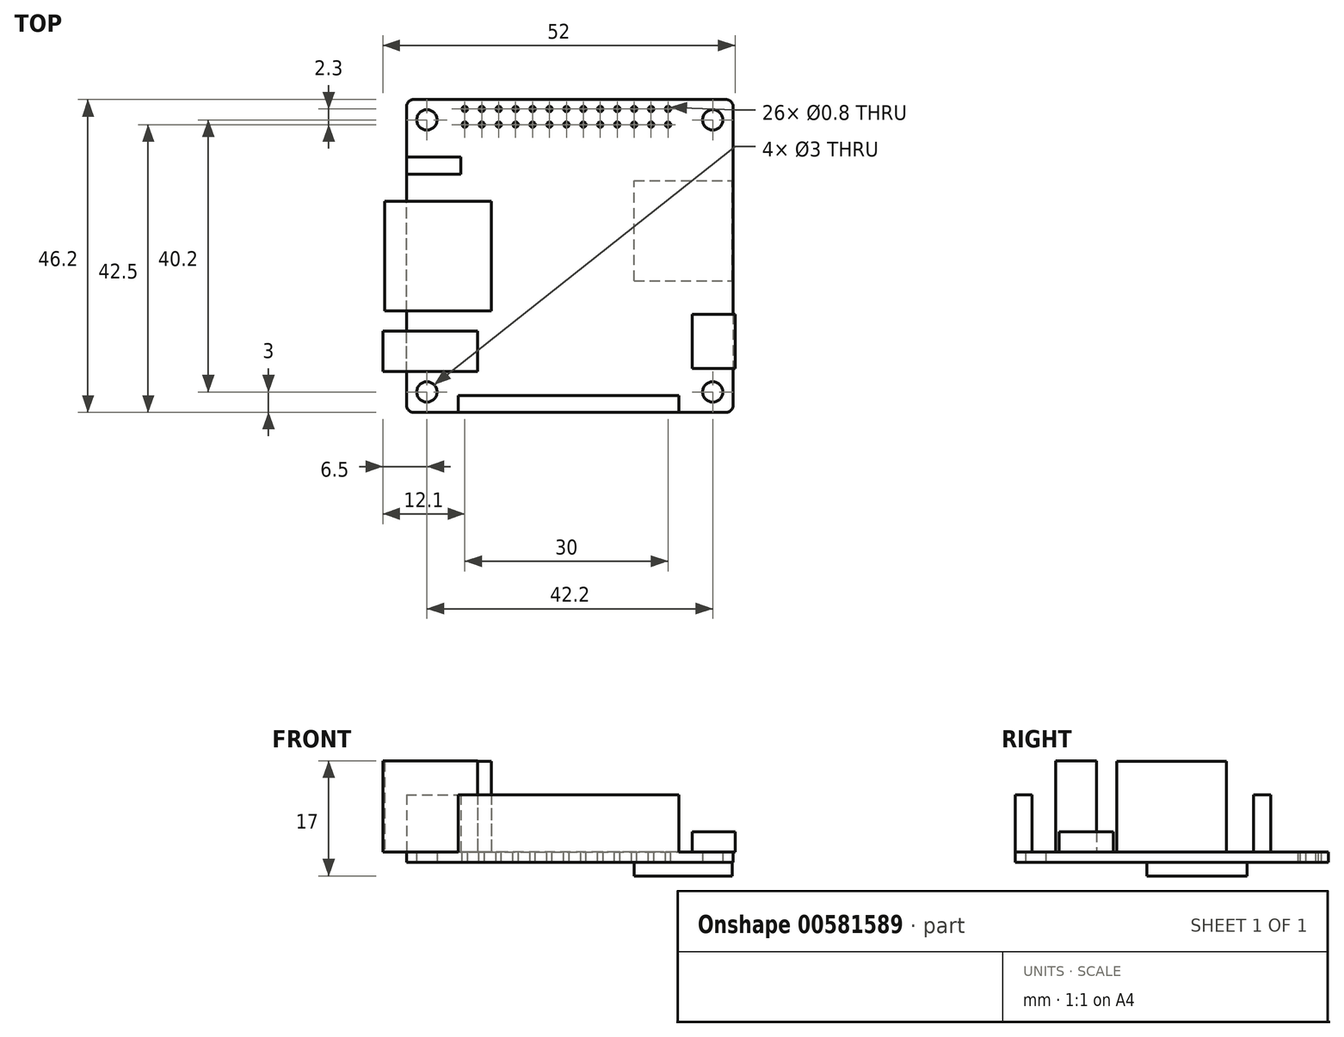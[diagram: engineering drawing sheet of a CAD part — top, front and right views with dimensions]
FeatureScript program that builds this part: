
annotation { "Feature Type Name" : "Feature", "Feature Type Description" : "" }
export const myFeature = defineFeature(function(context is Context, id is Id, definition is map)
    precondition{}
    {
        {
            var Q0;
            Q0=qCreatedBy(makeId("Top.planeOp"),FACE);
            var sketch = newSketch(context, id + "F0", { "sketchPlane" : qUnion([Q0])});
            skLineSegment(sketch, "E0.bottom", {"start": v(23.1, -23.1) * mm, "end": v(-23.1, -23.1) * mm});
            skLineSegment(sketch, "E0.top", {"start": v(23.1, 23.1) * mm, "end": v(-23.1, 23.1) * mm});
            skLineSegment(sketch, "E0.left", {"start": v(24.1, -22.1) * mm, "end": v(24.1, 22.1) * mm});
            skLineSegment(sketch, "E0.right", {"start": v(-24.1, -22.1) * mm, "end": v(-24.1, 22.1) * mm});
            skPoint(sketch, "E0.middle", {"position": v(0, 0) * mm});
            skPoint(sketch, "E1.visualSharp", {"position": v(-24.1, 23.1) * mm});
            skArc(sketch, "E1.filletArc", {"start": v(-23.1, 23.1) * mm, "mid": v(-23.8, 22.8) * mm, "end": v(-24.1, 22.1) * mm});
            skPoint(sketch, "E2.visualSharp", {"position": v(24.1, 23.1) * mm});
            skArc(sketch, "E2.filletArc", {"start": v(24.1, 22.1) * mm, "mid": v(23.8, 22.8) * mm, "end": v(23.1, 23.1) * mm});
            skPoint(sketch, "E3.visualSharp", {"position": v(24.1, -23.1) * mm});
            skArc(sketch, "E3.filletArc", {"start": v(23.1, -23.1) * mm, "mid": v(23.8, -22.8) * mm, "end": v(24.1, -22.1) * mm});
            skPoint(sketch, "E4.visualSharp", {"position": v(-24.1, -23.1) * mm});
            skArc(sketch, "E4.filletArc", {"start": v(-24.1, -22.1) * mm, "mid": v(-23.8, -22.8) * mm, "end": v(-23.1, -23.1) * mm});
            skCircle(sketch, "E5", {"center": v(-21.1, 20.1) * mm, "radius": 1.5 * mm});
            skCircle(sketch, "E6", {"center": v(21.1, 20.1) * mm, "radius": 1.5 * mm});
            skCircle(sketch, "E7", {"center": v(21.1, -20.1) * mm, "radius": 1.5 * mm});
            skCircle(sketch, "E8", {"center": v(-21.1, -20.1) * mm, "radius": 1.5 * mm});
            skSolve(sketch);
        }
        {
            var Q0;
            Q0=makeQuery(id+"F0.imprint","IMPRINT",FACE,{"disambiguationData":[TD([[makeQuery(id+"F0.imprint","IMPRINT",EDGE,{"derivedFrom":sQuery(id+"F0.wireOp",EDGE,"E0.bottom")}),-1.0]])]});
            extrude(context, id + "F1", {"entities" : qUnion([Q0]), "depth" : 1.5 * mm, "offsetDistance" : 25 * mm});
        }
        {
            var Q0;
            Q0=makeQuery(id+"F1.opExtrude","CAP_FACE",FACE,{"disambiguationData":[OSD([sQuery(id+"F0.wireOp",EDGE,"E0.bottom"),sQuery(id+"F0.wireOp",EDGE,"E0.top"),sQuery(id+"F0.wireOp",EDGE,"E0.left"),sQuery(id+"F0.wireOp",EDGE,"E0.right"),sQuery(id+"F0.wireOp",EDGE,"E1.filletArc"),sQuery(id+"F0.wireOp",EDGE,"E2.filletArc"),sQuery(id+"F0.wireOp",EDGE,"E3.filletArc"),sQuery(id+"F0.wireOp",EDGE,"E4.filletArc"),sQuery(id+"F0.wireOp",EDGE,"E5"),sQuery(id+"F0.wireOp",EDGE,"E6"),sQuery(id+"F0.wireOp",EDGE,"E7"),sQuery(id+"F0.wireOp",EDGE,"E8")])],"isStart":false});
            var sketch = newSketch(context, id + "F2", { "sketchPlane" : qUnion([Q0])});
            skLineSegment(sketch, "E9.bottom", {"start": v(-16.5, -23.1) * mm, "end": v(16.1, -23.1) * mm});
            skLineSegment(sketch, "E9.top", {"start": v(-16.5, -20.6) * mm, "end": v(16.1, -20.6) * mm});
            skLineSegment(sketch, "E9.left", {"start": v(-16.5, -23.1) * mm, "end": v(-16.5, -20.6) * mm});
            skLineSegment(sketch, "E9.right", {"start": v(16.1, -23.1) * mm, "end": v(16.1, -20.6) * mm});
            skSolve(sketch);
        }
        {
            var Q0;
            Q0=makeQuery(id+"F2.imprint","IMPRINT",FACE,{"disambiguationData":[TD([[makeQuery(id+"F2.imprint","IMPRINT",EDGE,{"derivedFrom":sQuery(id+"F2.wireOp",EDGE,"E9.bottom")}),-1.0]])]});
            extrude(context, id + "F3", {"entities" : qUnion([Q0]), "operationType" : NewBodyOperationType.ADD, "depth" : 8.5 * mm, "offsetDistance" : 25 * mm});
        }
        {
            var Q0;
            Q0=makeQuery(id+"F1.opExtrude","CAP_FACE",FACE,{"disambiguationData":[OSD([sQuery(id+"F0.wireOp",EDGE,"E0.bottom"),sQuery(id+"F0.wireOp",EDGE,"E0.top"),sQuery(id+"F0.wireOp",EDGE,"E0.left"),sQuery(id+"F0.wireOp",EDGE,"E0.right"),sQuery(id+"F0.wireOp",EDGE,"E1.filletArc"),sQuery(id+"F0.wireOp",EDGE,"E2.filletArc"),sQuery(id+"F0.wireOp",EDGE,"E3.filletArc"),sQuery(id+"F0.wireOp",EDGE,"E4.filletArc"),sQuery(id+"F0.wireOp",EDGE,"E5"),sQuery(id+"F0.wireOp",EDGE,"E6"),sQuery(id+"F0.wireOp",EDGE,"E7"),sQuery(id+"F0.wireOp",EDGE,"E8")])],"isStart":false});
            var sketch = newSketch(context, id + "F4", { "sketchPlane" : qUnion([Q0])});
            skLineSegment(sketch, "E10.bottom", {"start": v(24.1, -8.6) * mm, "end": v(18.1, -8.6) * mm});
            skLineSegment(sketch, "E10.top", {"start": v(24.1, -16.6) * mm, "end": v(18.1, -16.6) * mm});
            skLineSegment(sketch, "E10.left", {"start": v(24.1, -8.6) * mm, "end": v(24.1, -16.6) * mm});
            skLineSegment(sketch, "E10.right", {"start": v(18.1, -8.6) * mm, "end": v(18.1, -16.6) * mm});
            skSolve(sketch);
        }
        {
            var Q0;
            Q0=makeQuery(id+"F4.imprint","IMPRINT",FACE,{"disambiguationData":[TD([[makeQuery(id+"F4.imprint","IMPRINT",EDGE,{"derivedFrom":sQuery(id+"F4.wireOp",EDGE,"E10.bottom")}),1.0]])]});
            extrude(context, id + "F5", {"entities" : qUnion([Q0]), "operationType" : NewBodyOperationType.ADD, "depth" : 3 * mm, "offsetDistance" : 25 * mm});
        }
        {
            var Q0;
            Q0=makeQuery(id+"F5.boolean.opBoolean","MERGE",FACE,{"derivedFrom":[makeQuery(id+"F1.opExtrude","SWEPT_FACE",FACE,{"disambiguationData":[OSD([sQuery(id+"F0.wireOp",EDGE,"E0.left")])]}),makeQuery(id+"F5.opExtrude","SWEPT_FACE",FACE,{"disambiguationData":[OSD([sQuery(id+"F4.wireOp",EDGE,"E10.left")])]})]});
            var sketch = newSketch(context, id + "F6", { "sketchPlane" : qUnion([Q0])});
            skLineSegment(sketch, "E11", {"start": v(-8.6, 1.5) * mm, "end": v(-16.6, 1.5) * mm});
            skSolve(sketch);
        }
        {
            var Q0;
            Q0=makeQuery(id+"F6.imprint","IMPRINT",FACE,{"disambiguationData":[TD([[makeQuery(id+"F6.imprint","IMPRINT",EDGE,{"derivedFrom":sQuery(id+"F6.wireOp",EDGE,"E11")}),-1.0]])]});
            extrude(context, id + "F7", {"entities" : qUnion([Q0]), "operationType" : NewBodyOperationType.ADD, "depth" : 0.3 * mm, "offsetDistance" : 25 * mm});
        }
        {
            var Q0;
            Q0=makeQuery(id+"F1.opExtrude","CAP_FACE",FACE,{"disambiguationData":[OSD([sQuery(id+"F0.wireOp",EDGE,"E0.bottom"),sQuery(id+"F0.wireOp",EDGE,"E0.top"),sQuery(id+"F0.wireOp",EDGE,"E0.left"),sQuery(id+"F0.wireOp",EDGE,"E0.right"),sQuery(id+"F0.wireOp",EDGE,"E1.filletArc"),sQuery(id+"F0.wireOp",EDGE,"E2.filletArc"),sQuery(id+"F0.wireOp",EDGE,"E3.filletArc"),sQuery(id+"F0.wireOp",EDGE,"E4.filletArc"),sQuery(id+"F0.wireOp",EDGE,"E5"),sQuery(id+"F0.wireOp",EDGE,"E6"),sQuery(id+"F0.wireOp",EDGE,"E7"),sQuery(id+"F0.wireOp",EDGE,"E8")])],"isStart":false});
            var sketch = newSketch(context, id + "F8", { "sketchPlane" : qUnion([Q0])});
            skLineSegment(sketch, "E12.bottom", {"start": v(-16.4, 23.1) * mm, "end": v(16.1, 23.1) * mm});
            skLineSegment(sketch, "E12.top", {"start": v(-16.4, 18.1) * mm, "end": v(16.1, 18.1) * mm});
            skLineSegment(sketch, "E12.left", {"start": v(-16.4, 23.1) * mm, "end": v(-16.4, 18.1) * mm});
            skLineSegment(sketch, "E12.right", {"start": v(16.1, 23.1) * mm, "end": v(16.1, 18.1) * mm});
            skCircle(sketch, "E13", {"center": v(-15.5, 21.7) * mm, "radius": 0.4 * mm});
            skCircle(sketch, "E14", {"center": v(-15.5, 19.4) * mm, "radius": 0.4 * mm});
            skCircle(sketch, "E15.1.0.0", {"center": v(-13, 21.7) * mm, "radius": 0.4 * mm});
            skCircle(sketch, "E15.1.0.1", {"center": v(-13, 19.4) * mm, "radius": 0.4 * mm});
            skCircle(sketch, "E15.2.0.0", {"center": v(-10.5, 21.7) * mm, "radius": 0.4 * mm});
            skCircle(sketch, "E15.2.0.1", {"center": v(-10.5, 19.4) * mm, "radius": 0.4 * mm});
            skCircle(sketch, "E15.3.0.0", {"center": v(-8, 21.7) * mm, "radius": 0.4 * mm});
            skCircle(sketch, "E15.3.0.1", {"center": v(-8, 19.4) * mm, "radius": 0.4 * mm});
            skCircle(sketch, "E15.4.0.0", {"center": v(-5.5, 21.7) * mm, "radius": 0.4 * mm});
            skCircle(sketch, "E15.4.0.1", {"center": v(-5.5, 19.4) * mm, "radius": 0.4 * mm});
            skCircle(sketch, "E15.5.0.0", {"center": v(-3, 21.7) * mm, "radius": 0.4 * mm});
            skCircle(sketch, "E15.5.0.1", {"center": v(-3, 19.4) * mm, "radius": 0.4 * mm});
            skCircle(sketch, "E15.6.0.0", {"center": v(-0.5, 21.7) * mm, "radius": 0.4 * mm});
            skCircle(sketch, "E15.6.0.1", {"center": v(-0.5, 19.4) * mm, "radius": 0.4 * mm});
            skCircle(sketch, "E15.7.0.0", {"center": v(2, 21.7) * mm, "radius": 0.4 * mm});
            skCircle(sketch, "E15.7.0.1", {"center": v(2, 19.4) * mm, "radius": 0.4 * mm});
            skCircle(sketch, "E15.8.0.0", {"center": v(4.5, 21.7) * mm, "radius": 0.4 * mm});
            skCircle(sketch, "E15.8.0.1", {"center": v(4.5, 19.4) * mm, "radius": 0.4 * mm});
            skCircle(sketch, "E15.9.0.0", {"center": v(7, 21.7) * mm, "radius": 0.4 * mm});
            skCircle(sketch, "E15.9.0.1", {"center": v(7, 19.4) * mm, "radius": 0.4 * mm});
            skCircle(sketch, "E15.10.0.0", {"center": v(9.5, 21.7) * mm, "radius": 0.4 * mm});
            skCircle(sketch, "E15.10.0.1", {"center": v(9.5, 19.4) * mm, "radius": 0.4 * mm});
            skCircle(sketch, "E15.11.0.0", {"center": v(12, 21.7) * mm, "radius": 0.4 * mm});
            skCircle(sketch, "E15.11.0.1", {"center": v(12, 19.4) * mm, "radius": 0.4 * mm});
            skCircle(sketch, "E15.12.0.0", {"center": v(14.5, 21.7) * mm, "radius": 0.4 * mm});
            skCircle(sketch, "E15.12.0.1", {"center": v(14.5, 19.4) * mm, "radius": 0.4 * mm});
            skLineSegment(sketch, "E15.direction1", {"start": v(-15.5, 19.4) * mm, "end": v(-13, 19.4) * mm, "construction": true});
            skSolve(sketch);
        }
        {
            var Q0;
            Q0=makeQuery(id+"F8.imprint","IMPRINT",FACE,{"disambiguationData":[TD([[makeQuery(id+"F8.imprint","IMPRINT",EDGE,{"derivedFrom":sQuery(id+"F8.wireOp",EDGE,"E15.1.0.0")}),1.0]])]});
            var Q1;
            Q1=makeQuery(id+"F8.imprint","IMPRINT",FACE,{"disambiguationData":[TD([[makeQuery(id+"F8.imprint","IMPRINT",EDGE,{"derivedFrom":sQuery(id+"F8.wireOp",EDGE,"E13")}),1.0]])]});
            var Q2;
            Q2=makeQuery(id+"F8.imprint","IMPRINT",FACE,{"disambiguationData":[TD([[makeQuery(id+"F8.imprint","IMPRINT",EDGE,{"derivedFrom":sQuery(id+"F8.wireOp",EDGE,"E15.2.0.0")}),1.0]])]});
            var Q3;
            Q3=makeQuery(id+"F8.imprint","IMPRINT",FACE,{"disambiguationData":[TD([[makeQuery(id+"F8.imprint","IMPRINT",EDGE,{"derivedFrom":sQuery(id+"F8.wireOp",EDGE,"E15.3.0.0")}),1.0]])]});
            var Q4;
            Q4=makeQuery(id+"F8.imprint","IMPRINT",FACE,{"disambiguationData":[TD([[makeQuery(id+"F8.imprint","IMPRINT",EDGE,{"derivedFrom":sQuery(id+"F8.wireOp",EDGE,"E15.4.0.0")}),1.0]])]});
            var Q5;
            Q5=makeQuery(id+"F8.imprint","IMPRINT",FACE,{"disambiguationData":[TD([[makeQuery(id+"F8.imprint","IMPRINT",EDGE,{"derivedFrom":sQuery(id+"F8.wireOp",EDGE,"E15.5.0.0")}),1.0]])]});
            var Q6;
            Q6=makeQuery(id+"F8.imprint","IMPRINT",FACE,{"disambiguationData":[TD([[makeQuery(id+"F8.imprint","IMPRINT",EDGE,{"derivedFrom":sQuery(id+"F8.wireOp",EDGE,"E15.6.0.0")}),1.0]])]});
            var Q7;
            Q7=makeQuery(id+"F8.imprint","IMPRINT",FACE,{"disambiguationData":[TD([[makeQuery(id+"F8.imprint","IMPRINT",EDGE,{"derivedFrom":sQuery(id+"F8.wireOp",EDGE,"E15.7.0.0")}),1.0]])]});
            var Q8;
            Q8=makeQuery(id+"F8.imprint","IMPRINT",FACE,{"disambiguationData":[TD([[makeQuery(id+"F8.imprint","IMPRINT",EDGE,{"derivedFrom":sQuery(id+"F8.wireOp",EDGE,"E15.8.0.0")}),1.0]])]});
            var Q9;
            Q9=makeQuery(id+"F8.imprint","IMPRINT",FACE,{"disambiguationData":[TD([[makeQuery(id+"F8.imprint","IMPRINT",EDGE,{"derivedFrom":sQuery(id+"F8.wireOp",EDGE,"E15.9.0.0")}),1.0]])]});
            var Q10;
            Q10=makeQuery(id+"F8.imprint","IMPRINT",FACE,{"disambiguationData":[TD([[makeQuery(id+"F8.imprint","IMPRINT",EDGE,{"derivedFrom":sQuery(id+"F8.wireOp",EDGE,"E15.10.0.0")}),1.0]])]});
            var Q11;
            Q11=makeQuery(id+"F8.imprint","IMPRINT",FACE,{"disambiguationData":[TD([[makeQuery(id+"F8.imprint","IMPRINT",EDGE,{"derivedFrom":sQuery(id+"F8.wireOp",EDGE,"E15.11.0.0")}),1.0]])]});
            var Q12;
            Q12=makeQuery(id+"F8.imprint","IMPRINT",FACE,{"disambiguationData":[TD([[makeQuery(id+"F8.imprint","IMPRINT",EDGE,{"derivedFrom":sQuery(id+"F8.wireOp",EDGE,"E15.12.0.0")}),1.0]])]});
            var Q13;
            Q13=makeQuery(id+"F8.imprint","IMPRINT",FACE,{"disambiguationData":[TD([[makeQuery(id+"F8.imprint","IMPRINT",EDGE,{"derivedFrom":sQuery(id+"F8.wireOp",EDGE,"E15.12.0.1")}),1.0]])]});
            var Q14;
            Q14=makeQuery(id+"F8.imprint","IMPRINT",FACE,{"disambiguationData":[TD([[makeQuery(id+"F8.imprint","IMPRINT",EDGE,{"derivedFrom":sQuery(id+"F8.wireOp",EDGE,"E15.11.0.1")}),1.0]])]});
            var Q15;
            Q15=makeQuery(id+"F8.imprint","IMPRINT",FACE,{"disambiguationData":[TD([[makeQuery(id+"F8.imprint","IMPRINT",EDGE,{"derivedFrom":sQuery(id+"F8.wireOp",EDGE,"E15.10.0.1")}),1.0]])]});
            var Q16;
            Q16=makeQuery(id+"F8.imprint","IMPRINT",FACE,{"disambiguationData":[TD([[makeQuery(id+"F8.imprint","IMPRINT",EDGE,{"derivedFrom":sQuery(id+"F8.wireOp",EDGE,"E15.9.0.1")}),1.0]])]});
            var Q17;
            Q17=makeQuery(id+"F8.imprint","IMPRINT",FACE,{"disambiguationData":[TD([[makeQuery(id+"F8.imprint","IMPRINT",EDGE,{"derivedFrom":sQuery(id+"F8.wireOp",EDGE,"E15.8.0.1")}),1.0]])]});
            var Q18;
            Q18=makeQuery(id+"F8.imprint","IMPRINT",FACE,{"disambiguationData":[TD([[makeQuery(id+"F8.imprint","IMPRINT",EDGE,{"derivedFrom":sQuery(id+"F8.wireOp",EDGE,"E15.7.0.1")}),1.0]])]});
            var Q19;
            Q19=makeQuery(id+"F8.imprint","IMPRINT",FACE,{"disambiguationData":[TD([[makeQuery(id+"F8.imprint","IMPRINT",EDGE,{"derivedFrom":sQuery(id+"F8.wireOp",EDGE,"E15.6.0.1")}),1.0]])]});
            var Q20;
            Q20=makeQuery(id+"F8.imprint","IMPRINT",FACE,{"disambiguationData":[TD([[makeQuery(id+"F8.imprint","IMPRINT",EDGE,{"derivedFrom":sQuery(id+"F8.wireOp",EDGE,"E15.5.0.1")}),1.0]])]});
            var Q21;
            Q21=makeQuery(id+"F8.imprint","IMPRINT",FACE,{"disambiguationData":[TD([[makeQuery(id+"F8.imprint","IMPRINT",EDGE,{"derivedFrom":sQuery(id+"F8.wireOp",EDGE,"E15.4.0.1")}),1.0]])]});
            var Q22;
            Q22=makeQuery(id+"F8.imprint","IMPRINT",FACE,{"disambiguationData":[TD([[makeQuery(id+"F8.imprint","IMPRINT",EDGE,{"derivedFrom":sQuery(id+"F8.wireOp",EDGE,"E15.3.0.1")}),1.0]])]});
            var Q23;
            Q23=makeQuery(id+"F8.imprint","IMPRINT",FACE,{"disambiguationData":[TD([[makeQuery(id+"F8.imprint","IMPRINT",EDGE,{"derivedFrom":sQuery(id+"F8.wireOp",EDGE,"E15.2.0.1")}),1.0]])]});
            var Q24;
            Q24=makeQuery(id+"F8.imprint","IMPRINT",FACE,{"disambiguationData":[TD([[makeQuery(id+"F8.imprint","IMPRINT",EDGE,{"derivedFrom":sQuery(id+"F8.wireOp",EDGE,"E15.1.0.1")}),1.0]])]});
            var Q25;
            Q25=makeQuery(id+"F8.imprint","IMPRINT",FACE,{"disambiguationData":[TD([[makeQuery(id+"F8.imprint","IMPRINT",EDGE,{"derivedFrom":sQuery(id+"F8.wireOp",EDGE,"E14")}),1.0]])]});
            extrude(context, id + "F9", {"entities" : qUnion([Q0, Q1, Q2, Q3, Q4, Q5, Q6, Q7, Q8, Q9, Q10, Q11, Q12, Q13, Q14, Q15, Q16, Q17, Q18, Q19, Q20, Q21, Q22, Q23, Q24, Q25]), "operationType" : NewBodyOperationType.REMOVE, "endBound" : BoundingType.UP_TO_NEXT, "oppositeDirection" : true, "depth" : 25 * mm, "offsetDistance" : 25 * mm});
        }
        {
            var Q0;
            Q0=makeQuery(id+"F1.opExtrude","CAP_FACE",FACE,{"disambiguationData":[OSD([sQuery(id+"F0.wireOp",EDGE,"E0.bottom"),sQuery(id+"F0.wireOp",EDGE,"E0.top"),sQuery(id+"F0.wireOp",EDGE,"E0.left"),sQuery(id+"F0.wireOp",EDGE,"E0.right"),sQuery(id+"F0.wireOp",EDGE,"E1.filletArc"),sQuery(id+"F0.wireOp",EDGE,"E2.filletArc"),sQuery(id+"F0.wireOp",EDGE,"E3.filletArc"),sQuery(id+"F0.wireOp",EDGE,"E4.filletArc"),sQuery(id+"F0.wireOp",EDGE,"E5"),sQuery(id+"F0.wireOp",EDGE,"E6"),sQuery(id+"F0.wireOp",EDGE,"E7"),sQuery(id+"F0.wireOp",EDGE,"E8")])],"isStart":false});
            var sketch = newSketch(context, id + "F10", { "sketchPlane" : qUnion([Q0])});
            skLineSegment(sketch, "E16.bottom", {"start": v(-24.1, 14.6) * mm, "end": v(-16.1, 14.6) * mm});
            skLineSegment(sketch, "E16.top", {"start": v(-24.1, 12.1) * mm, "end": v(-16.1, 12.1) * mm});
            skLineSegment(sketch, "E16.left", {"start": v(-24.1, 14.6) * mm, "end": v(-24.1, 12.1) * mm});
            skLineSegment(sketch, "E16.right", {"start": v(-16.1, 14.6) * mm, "end": v(-16.1, 12.1) * mm});
            skSolve(sketch);
        }
        {
            var Q0;
            Q0 = qSketchRegion(id + "F10", true);
            extrude(context, id + "F11", {"entities" : qUnion([Q0]), "operationType" : NewBodyOperationType.ADD, "depth" : 8.5 * mm, "offsetDistance" : 25 * mm});
        }
        {
            var Q0;
            Q0=makeQuery(id+"F1.opExtrude","CAP_FACE",FACE,{"disambiguationData":[OSD([sQuery(id+"F0.wireOp",EDGE,"E0.bottom"),sQuery(id+"F0.wireOp",EDGE,"E0.top"),sQuery(id+"F0.wireOp",EDGE,"E0.left"),sQuery(id+"F0.wireOp",EDGE,"E0.right"),sQuery(id+"F0.wireOp",EDGE,"E1.filletArc"),sQuery(id+"F0.wireOp",EDGE,"E2.filletArc"),sQuery(id+"F0.wireOp",EDGE,"E3.filletArc"),sQuery(id+"F0.wireOp",EDGE,"E4.filletArc"),sQuery(id+"F0.wireOp",EDGE,"E5"),sQuery(id+"F0.wireOp",EDGE,"E6"),sQuery(id+"F0.wireOp",EDGE,"E7"),sQuery(id+"F0.wireOp",EDGE,"E8")])],"isStart":false});
            var sketch = newSketch(context, id + "F12", { "sketchPlane" : qUnion([Q0])});
            skLineSegment(sketch, "E17.bottom", {"start": v(-27.35, 8.1) * mm, "end": v(-11.6, 8.1) * mm});
            skLineSegment(sketch, "E17.top", {"start": v(-27.35, -8.1) * mm, "end": v(-11.6, -8.1) * mm});
            skLineSegment(sketch, "E17.left", {"start": v(-27.35, 8.1) * mm, "end": v(-27.35, -8.1) * mm});
            skLineSegment(sketch, "E17.right", {"start": v(-11.6, 8.1) * mm, "end": v(-11.6, -8.1) * mm});
            skSolve(sketch);
        }
        {
            var Q0;
            {var subQ0=sQuery(id+"F12.wireOp",EDGE,"E17.left");Q0=makeQuery(id+"F12.imprint","IMPRINT",FACE,{"disambiguationData":[TD([[makeQuery(id+"F12.imprint","IMPRINT",EDGE,{"derivedFrom":subQ0}),1.0]])]});}
            var Q1;
            {var subQ0=sQuery(id+"F12.wireOp",EDGE,"E17.right");Q1=makeQuery(id+"F12.imprint","IMPRINT",FACE,{"disambiguationData":[TD([[makeQuery(id+"F12.imprint","IMPRINT",EDGE,{"derivedFrom":subQ0}),-1.0]])]});}
            extrude(context, id + "F13", {"entities" : qUnion([Q0, Q1]), "operationType" : NewBodyOperationType.ADD, "depth" : 13.4 * mm, "offsetDistance" : 25 * mm});
        }
        {
            var Q0;
            Q0=makeQuery(id+"F1.opExtrude","CAP_FACE",FACE,{"disambiguationData":[OSD([sQuery(id+"F0.wireOp",EDGE,"E0.bottom"),sQuery(id+"F0.wireOp",EDGE,"E0.top"),sQuery(id+"F0.wireOp",EDGE,"E0.left"),sQuery(id+"F0.wireOp",EDGE,"E0.right"),sQuery(id+"F0.wireOp",EDGE,"E1.filletArc"),sQuery(id+"F0.wireOp",EDGE,"E2.filletArc"),sQuery(id+"F0.wireOp",EDGE,"E3.filletArc"),sQuery(id+"F0.wireOp",EDGE,"E4.filletArc"),sQuery(id+"F0.wireOp",EDGE,"E5"),sQuery(id+"F0.wireOp",EDGE,"E6"),sQuery(id+"F0.wireOp",EDGE,"E7"),sQuery(id+"F0.wireOp",EDGE,"E8")])],"isStart":false});
            var sketch = newSketch(context, id + "F14", { "sketchPlane" : qUnion([Q0])});
            skLineSegment(sketch, "E18.bottom", {"start": v(-13.6, -11.1) * mm, "end": v(-27.6, -11.1) * mm});
            skLineSegment(sketch, "E18.top", {"start": v(-13.6, -17.1) * mm, "end": v(-27.6, -17.1) * mm});
            skLineSegment(sketch, "E18.left", {"start": v(-13.6, -11.1) * mm, "end": v(-13.6, -17.1) * mm});
            skLineSegment(sketch, "E18.right", {"start": v(-27.6, -11.1) * mm, "end": v(-27.6, -17.1) * mm});
            skSolve(sketch);
        }
        {
            var Q0;
            {var subQ0=sQuery(id+"F14.wireOp",EDGE,"E18.right");Q0=makeQuery(id+"F14.imprint","IMPRINT",FACE,{"disambiguationData":[TD([[makeQuery(id+"F14.imprint","IMPRINT",EDGE,{"derivedFrom":subQ0}),1.0]])]});}
            var Q1;
            {var subQ0=sQuery(id+"F14.wireOp",EDGE,"E18.left");Q1=makeQuery(id+"F14.imprint","IMPRINT",FACE,{"disambiguationData":[TD([[makeQuery(id+"F14.imprint","IMPRINT",EDGE,{"derivedFrom":subQ0}),-1.0]])]});}
            extrude(context, id + "F15", {"entities" : qUnion([Q0, Q1]), "operationType" : NewBodyOperationType.ADD, "depth" : 13.5 * mm, "offsetDistance" : 25 * mm});
        }
        {
            var Q0;
            Q0=makeQuery(id+"F1.opExtrude","CAP_FACE",FACE,{"disambiguationData":[OSD([sQuery(id+"F0.wireOp",EDGE,"E0.bottom"),sQuery(id+"F0.wireOp",EDGE,"E0.top"),sQuery(id+"F0.wireOp",EDGE,"E0.left"),sQuery(id+"F0.wireOp",EDGE,"E0.right"),sQuery(id+"F0.wireOp",EDGE,"E1.filletArc"),sQuery(id+"F0.wireOp",EDGE,"E2.filletArc"),sQuery(id+"F0.wireOp",EDGE,"E3.filletArc"),sQuery(id+"F0.wireOp",EDGE,"E4.filletArc"),sQuery(id+"F0.wireOp",EDGE,"E5"),sQuery(id+"F0.wireOp",EDGE,"E6"),sQuery(id+"F0.wireOp",EDGE,"E7"),sQuery(id+"F0.wireOp",EDGE,"E8")])],"isStart":true});
            var sketch = newSketch(context, id + "F16", { "sketchPlane" : qUnion([Q0])});
            skLineSegment(sketch, "E19.bottom", {"start": v(9.5, 3.65) * mm, "end": v(24.1, 3.65) * mm});
            skLineSegment(sketch, "E19.top", {"start": v(9.5, -11.1) * mm, "end": v(24.1, -11.1) * mm});
            skLineSegment(sketch, "E19.left", {"start": v(9.5, 3.65) * mm, "end": v(9.5, -11.1) * mm});
            skLineSegment(sketch, "E19.right", {"start": v(24.1, 3.65) * mm, "end": v(24.1, -11.1) * mm});
            skSolve(sketch);
        }
        {
            var Q0;
            Q0=makeQuery(id+"F16.imprint","IMPRINT",FACE,{"disambiguationData":[TD([[makeQuery(id+"F16.imprint","IMPRINT",EDGE,{"derivedFrom":sQuery(id+"F16.wireOp",EDGE,"E19.bottom")}),-1.0]])]});
            extrude(context, id + "F17", {"entities" : qUnion([Q0]), "operationType" : NewBodyOperationType.ADD, "depth" : 2 * mm, "offsetDistance" : 25 * mm});
        }
        {
            var Q0;
            Q0=makeQuery(id+"F17.boolean.opBoolean","MERGE",FACE,{"derivedFrom":[makeQuery(id+"F5.boolean.opBoolean","MERGE",FACE,{"derivedFrom":[makeQuery(id+"F1.opExtrude","SWEPT_FACE",FACE,{"disambiguationData":[OSD([sQuery(id+"F0.wireOp",EDGE,"E0.left")])]}),makeQuery(id+"F5.opExtrude","SWEPT_FACE",FACE,{"disambiguationData":[OSD([sQuery(id+"F4.wireOp",EDGE,"E10.left")])]})]}),makeQuery(id+"F17.opExtrude","SWEPT_FACE",FACE,{"disambiguationData":[OSD([sQuery(id+"F16.wireOp",EDGE,"E19.right")])]})]});
            var sketch = newSketch(context, id + "F18", { "sketchPlane" : qUnion([Q0])});
            skLineSegment(sketch, "E20", {"start": v(-3.65, 0) * mm, "end": v(11.1, 0) * mm});
            skSolve(sketch);
        }
        {
            var Q0;
            Q0=makeQuery(id+"F18.imprint","IMPRINT",FACE,{"disambiguationData":[TD([[makeQuery(id+"F18.imprint","IMPRINT",EDGE,{"derivedFrom":sQuery(id+"F18.wireOp",EDGE,"E20")}),-1.0]])]});
            extrude(context, id + "F19", {"entities" : qUnion([Q0]), "operationType" : NewBodyOperationType.REMOVE, "oppositeDirection" : true, "depth" : 0.1 * mm, "offsetDistance" : 25 * mm});
        }
    });
